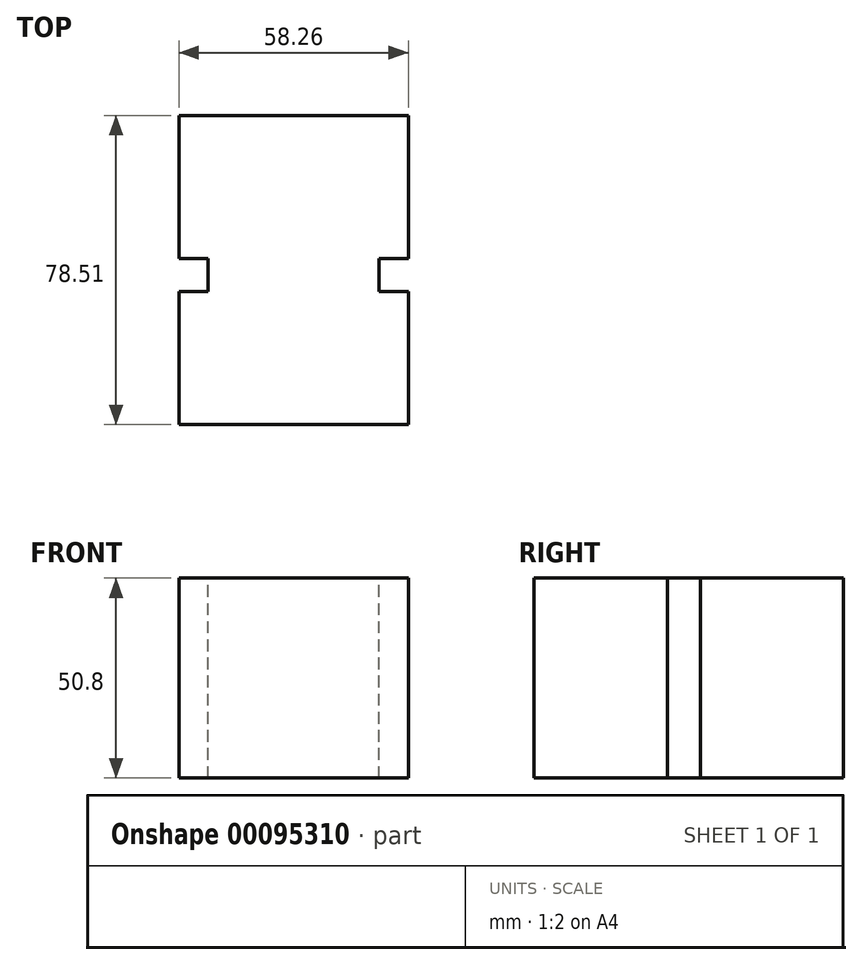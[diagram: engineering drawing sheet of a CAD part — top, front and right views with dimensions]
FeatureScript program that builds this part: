
annotation { "Feature Type Name" : "Feature", "Feature Type Description" : "" }
export const myFeature = defineFeature(function(context is Context, id is Id, definition is map)
    precondition{}
    {
        {
            var Q0;
            Q0=qCreatedBy(makeId("Top.planeOp"),FACE);
            var sketch = newSketch(context, id + "F0", { "sketchPlane" : qUnion([Q0])});
            skLineSegment(sketch, "E0.bottom", {"start": v(-29.7, 36.28) * mm, "end": v(28.56, 36.28) * mm});
            skLineSegment(sketch, "E0.top", {"start": v(-29.7, -42.23) * mm, "end": v(28.56, -42.23) * mm});
            skLineSegment(sketch, "E0.left", {"start": v(-29.7, 36.28) * mm, "end": v(-29.7, -42.23) * mm});
            skLineSegment(sketch, "E0.right", {"start": v(28.56, 36.28) * mm, "end": v(28.56, -42.23) * mm});
            skCircle(sketch, "E1", {"center": v(0, 10.93) * mm, "radius": 20.5 * mm});
            skCircle(sketch, "E2", {"center": v(0, -19.57) * mm, "radius": 10 * mm});
            skCircle(sketch, "E3", {"center": v(0, -34.57) * mm, "radius": 5 * mm});
            skLineSegment(sketch, "E4.bottom", {"start": v(-29.7, 0) * mm, "end": v(-22.25, 0) * mm});
            skLineSegment(sketch, "E4.top", {"start": v(-29.7, -8.41) * mm, "end": v(-22.25, -8.41) * mm});
            skLineSegment(sketch, "E4.left", {"start": v(-29.7, 0) * mm, "end": v(-29.7, -8.41) * mm});
            skLineSegment(sketch, "E4.right", {"start": v(-22.25, 0) * mm, "end": v(-22.25, -8.41) * mm});
            skLineSegment(sketch, "E5.bottom", {"start": v(28.56, 0) * mm, "end": v(21.1, 0) * mm});
            skLineSegment(sketch, "E5.top", {"start": v(28.56, -8.41) * mm, "end": v(21.1, -8.41) * mm});
            skLineSegment(sketch, "E5.left", {"start": v(28.56, 0) * mm, "end": v(28.56, -8.41) * mm});
            skLineSegment(sketch, "E5.right", {"start": v(21.1, 0) * mm, "end": v(21.1, -8.41) * mm});
            skSolve(sketch);
        }
        {
            var Q0;
            {var subQ5=sQuery(id+"F0.wireOp",EDGE,"E0.bottom");Q0=makeQuery(id+"F0.imprint","IMPRINT",FACE,{"disambiguationData":[TD([[makeQuery(id+"F0.imprint","IMPRINT",EDGE,{"derivedFrom":subQ5}),-1.0]])]});}
            var Q1;
            Q1=makeQuery(id+"F0.imprint","IMPRINT",FACE,{"disambiguationData":[TD([[makeQuery(id+"F0.imprint","IMPRINT",EDGE,{"derivedFrom":sQuery(id+"F0.wireOp",EDGE,"E1")}),1.0]])]});
            var Q2;
            {var subQ0=sQuery(id+"F0.wireOp",EDGE,"E2");var subQ1=makeQuery(id+"F0.imprint","INTERSECT",VERTEX,{"derivedFrom":[sQuery(id+"F0.wireOp",EDGE,"E1"),subQ0]});Q2=makeQuery(id+"F0.imprint","IMPRINT",FACE,{"disambiguationData":[TD([[makeQuery(id+"F0.imprint","IMPRINT",EDGE,{"disambiguationData":[TD([[subQ1,-1.0]])],"derivedFrom":subQ0}),1.0]])]});}
            var Q3;
            Q3=makeQuery(id+"F0.imprint","IMPRINT",FACE,{"disambiguationData":[TD([[makeQuery(id+"F0.imprint","IMPRINT",EDGE,{"derivedFrom":sQuery(id+"F0.wireOp",EDGE,"E3")}),1.0]])]});
            extrude(context, id + "F1", {"entities" : qUnion([Q0, Q1, Q2, Q3]), "oppositeDirection" : true, "depth" : 50.8 * mm});
        }
    });
